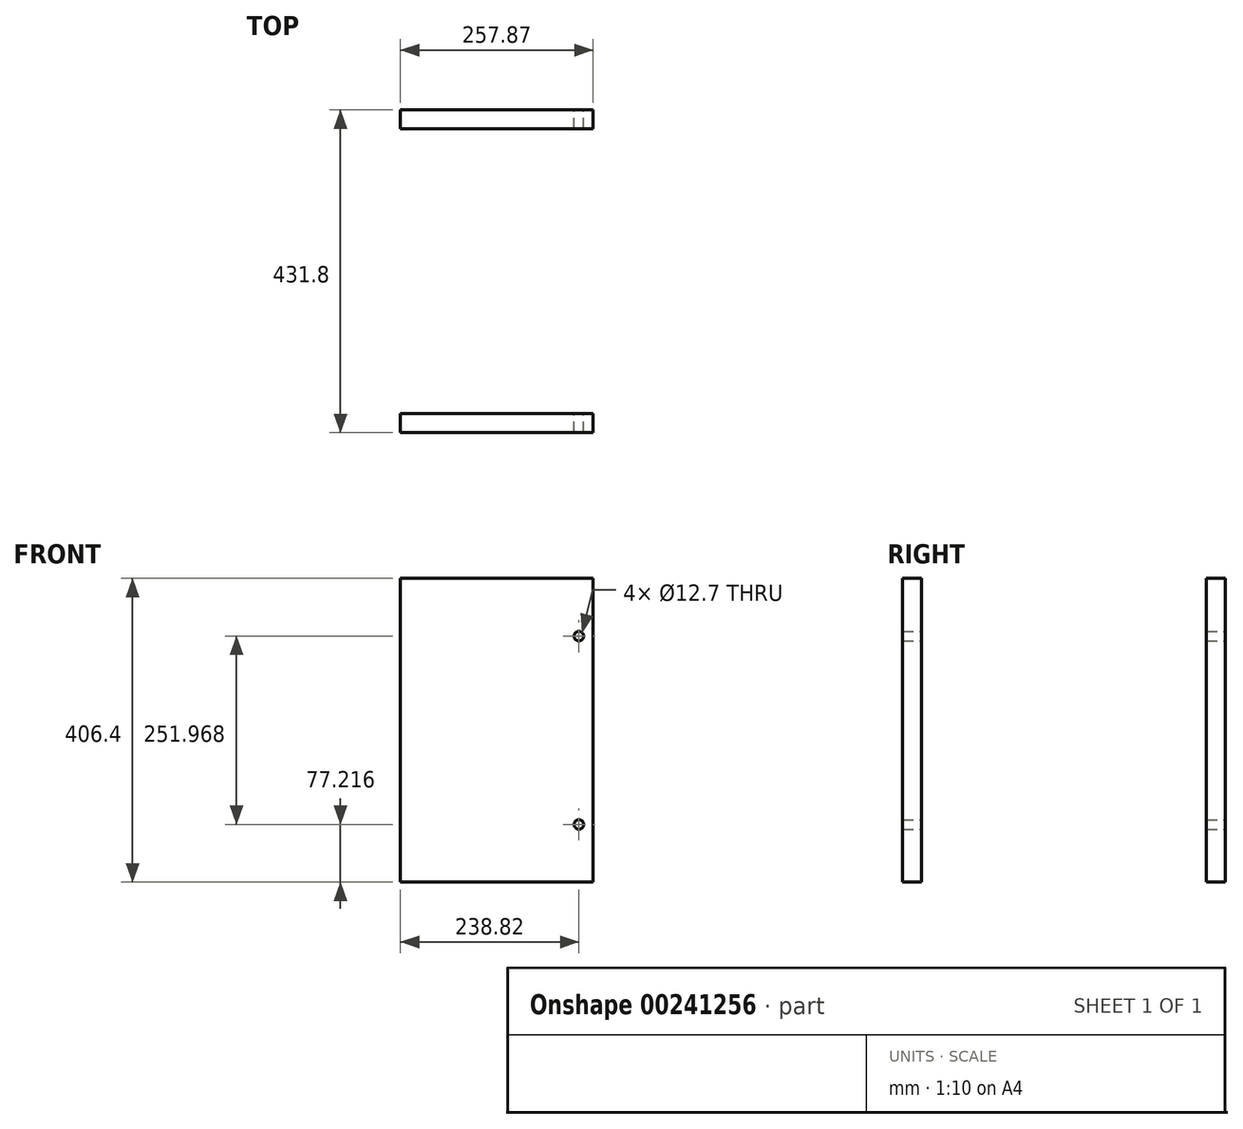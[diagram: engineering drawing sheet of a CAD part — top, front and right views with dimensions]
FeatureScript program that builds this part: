
annotation { "Feature Type Name" : "Feature", "Feature Type Description" : "" }
export const myFeature = defineFeature(function(context is Context, id is Id, definition is map)
    precondition{}
    {
        {
            var Q0;
            Q0=qCreatedBy(makeId("Front.planeOp"),FACE);
            var sketch = newSketch(context, id + "F0", { "sketchPlane" : qUnion([Q0])});
            skLineSegment(sketch, "E0", {"start": v(0, 125.98) * mm, "end": v(0, -125.98) * mm});
            skCircle(sketch, "E1", {"center": v(0, 125.98) * mm, "radius": 6.35 * mm});
            skCircle(sketch, "E2", {"center": v(0, -125.98) * mm, "radius": 6.35 * mm});
            skLineSegment(sketch, "E3", {"start": v(0, -125.98) * mm, "end": v(19.05, -125.98) * mm});
            skLineSegment(sketch, "E4", {"start": v(19.05, -203.2) * mm, "end": v(19.05, 0) * mm});
            skLineSegment(sketch, "E5", {"start": v(19.05, 0) * mm, "end": v(19.05, 203.2) * mm});
            skLineSegment(sketch, "E6", {"start": v(19.05, 203.2) * mm, "end": v(-238.82, 203.2) * mm});
            skLineSegment(sketch, "E7", {"start": v(19.05, -203.2) * mm, "end": v(-238.82, -203.2) * mm});
            skLineSegment(sketch, "E8", {"start": v(-238.82, -203.2) * mm, "end": v(-238.82, 203.2) * mm});
            skSolve(sketch);
        }
        {
            var Q0;
            Q0=makeQuery(id+"F0.imprint","IMPRINT",FACE,{"disambiguationData":[TD([[makeQuery(id+"F0.imprint","IMPRINT",EDGE,{"derivedFrom":sQuery(id+"F0.wireOp",EDGE,"E1")}),-1.0]])]});
            extrude(context, id + "F1", {"entities" : qUnion([Q0]), "depth" : 25.4 * mm});
        }
        {
            var Q0;
            Q0=makeQuery(id+"F1.opExtrude","SWEPT_BODY",BODY,{"disambiguationData":[OSD([sQuery(id+"F0.wireOp",EDGE,"E1"),sQuery(id+"F0.wireOp",EDGE,"E2"),sQuery(id+"F0.wireOp",EDGE,"E4"),sQuery(id+"F0.wireOp",EDGE,"E5"),sQuery(id+"F0.wireOp",EDGE,"E6"),sQuery(id+"F0.wireOp",EDGE,"E7"),sQuery(id+"F0.wireOp",EDGE,"E8")])]});
            transform(context, id + "F2", {"entities" : qUnion([Q0]), "transformType" : TransformType.TRANSLATION_3D, "dx" : 0 * mm, "dy" : 406.4 * mm, "dz" : 0 * mm, "makeCopy" : true});
        }
    });
